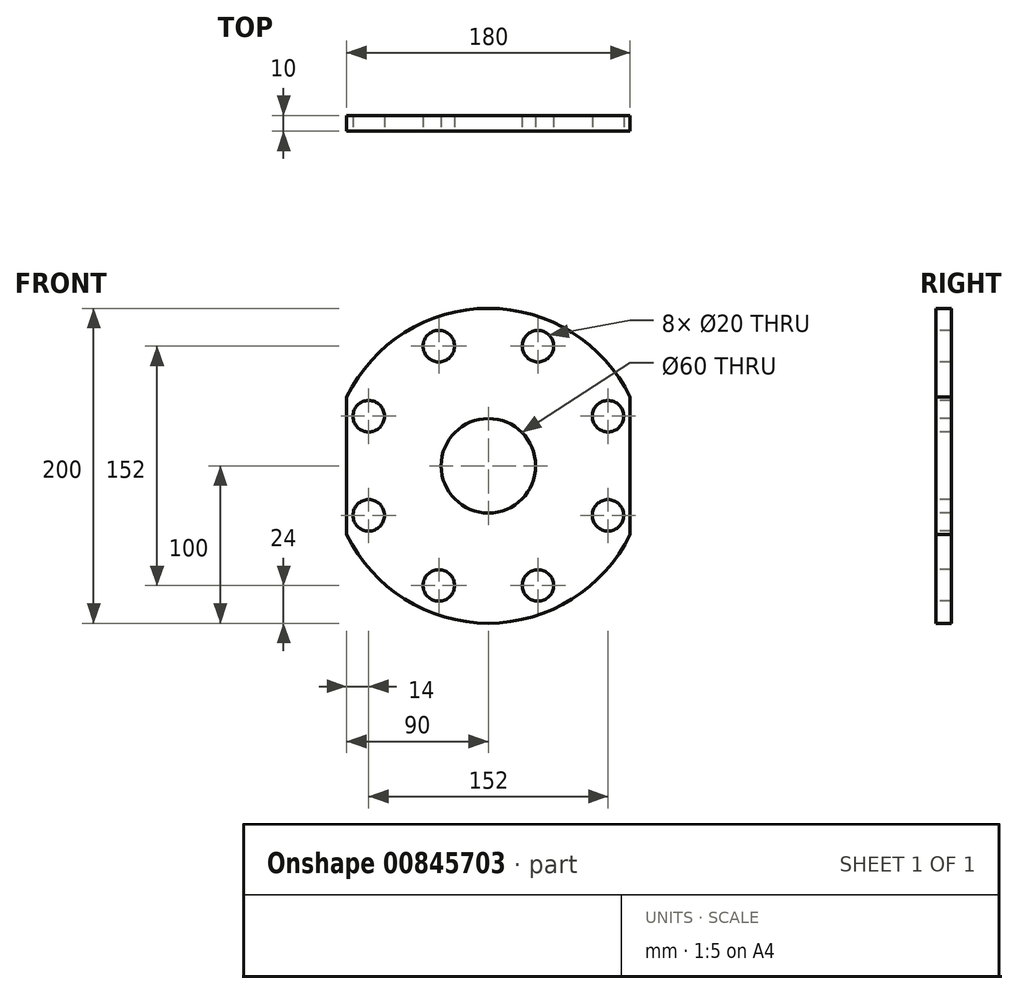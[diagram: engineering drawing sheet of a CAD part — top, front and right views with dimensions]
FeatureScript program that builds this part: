
annotation { "Feature Type Name" : "Feature", "Feature Type Description" : "" }
export const myFeature = defineFeature(function(context is Context, id is Id, definition is map)
    precondition{}
    {
        {
            var Q0;
            Q0=qCreatedBy(makeId("Front.planeOp"),FACE);
            var sketch = newSketch(context, id + "F0", { "sketchPlane" : qUnion([Q0])});
            skCircle(sketch, "E0", {"center": v(0, 0) * mm, "radius": 100 * mm});
            skSolve(sketch);
        }
        {
            var Q0;
            Q0=makeQuery(id+"F0.imprint","IMPRINT",FACE,{"disambiguationData":[TD([[makeQuery(id+"F0.imprint","IMPRINT",EDGE,{"derivedFrom":sQuery(id+"F0.wireOp",EDGE,"E0")}),1.0]])]});
            var sketch = newSketch(context, id + "F1", { "sketchPlane" : qUnion([Q0])});
            skLineSegment(sketch, "E1.bottom", {"start": v(90, 100) * mm, "end": v(-90, 100) * mm});
            skLineSegment(sketch, "E1.top", {"start": v(90, -100) * mm, "end": v(-90, -100) * mm});
            skLineSegment(sketch, "E1.left", {"start": v(90, 100) * mm, "end": v(90, -100) * mm});
            skLineSegment(sketch, "E1.right", {"start": v(-90, 100) * mm, "end": v(-90, -100) * mm});
            skPoint(sketch, "E1.middle", {"position": v(0, 0) * mm});
            skSolve(sketch);
        }
        {
            var Q0;
            Q0=qSketchRegion(id+"F0",true);
            extrude(context, id + "F2", {"entities" : qUnion([Q0]), "depth" : 10 * mm, "offsetDistance" : 25 * mm});
        }
        {
            var Q0;
            {var subQ0=sQuery(id+"F1.wireOp",EDGE,"E1.right");var subQ1=sQuery(id+"F1.wireOp",EDGE,"E1.bottom");var subQ2=makeQuery(id+"F1.imprint","INTERSECT",VERTEX,{"derivedFrom":[subQ1,subQ0]});Q0=makeQuery(id+"F1.imprint","IMPRINT",FACE,{"disambiguationData":[TD([[makeQuery(id+"F1.imprint","IMPRINT",EDGE,{"disambiguationData":[TD([[subQ2,1.0]])],"derivedFrom":subQ1}),1.0]])]});}
            var Q1;
            {var subQ0=sQuery(id+"F1.wireOp",EDGE,"E1.right");var subQ1=makeQuery(id+"F0.imprint","IMPRINT",EDGE,{"derivedFrom":sQuery(id+"F0.wireOp",EDGE,"E0")});var subQ2=makeQuery(id+"F1.imprint","INTERSECT",VERTEX,{"disambiguationData":[OD(0.0)],"derivedFrom":[subQ1,subQ0]});Q1=makeQuery(id+"F1.imprint","IMPRINT",FACE,{"disambiguationData":[TD([[makeQuery(id+"F1.imprint","IMPRINT",EDGE,{"disambiguationData":[TD([[subQ2,-1.0]])],"derivedFrom":subQ0}),-1.0]])]});}
            var Q2;
            {var subQ0=sQuery(id+"F1.wireOp",EDGE,"E1.left");var subQ1=makeQuery(id+"F0.imprint","IMPRINT",EDGE,{"derivedFrom":sQuery(id+"F0.wireOp",EDGE,"E0")});var subQ2=makeQuery(id+"F1.imprint","INTERSECT",VERTEX,{"disambiguationData":[OD(0.0)],"derivedFrom":[subQ1,subQ0]});Q2=makeQuery(id+"F1.imprint","IMPRINT",FACE,{"disambiguationData":[TD([[makeQuery(id+"F1.imprint","IMPRINT",EDGE,{"disambiguationData":[TD([[subQ2,-1.0]])],"derivedFrom":subQ0}),1.0]])]});}
            extrude(context, id + "F3", {"entities" : qUnion([Q0, Q1, Q2]), "operationType" : NewBodyOperationType.REMOVE, "endBound" : BoundingType.THROUGH_ALL, "depth" : 25 * mm, "offsetDistance" : 25 * mm});
        }
        {
            var Q0;
            Q0=makeQuery(id+"F2.opExtrude","CAP_FACE",FACE,{"disambiguationData":[OSD([sQuery(id+"F0.wireOp",EDGE,"E0")])],"isStart":false});
            var sketch = newSketch(context, id + "F4", { "sketchPlane" : qUnion([Q0])});
            skLineSegment(sketch, "E2", {"start": v(-90, 0) * mm, "end": v(90, 0) * mm, "construction": true});
            skLineSegment(sketch, "E3", {"start": v(0, 100) * mm, "end": v(0, -100) * mm, "construction": true});
            skCircle(sketch, "E4", {"center": v(-76, 31.48) * mm, "radius": 10 * mm});
            skLineSegment(sketch, "E5", {"start": v(70.71, -70.71) * mm, "end": v(0, 0) * mm, "construction": true});
            skLineSegment(sketch, "E6", {"start": v(0, 0) * mm, "end": v(-70.71, 70.71) * mm, "construction": true});
            skLineSegment(sketch, "E7", {"start": v(0, 0) * mm, "end": v(70.71, 70.71) * mm, "construction": true});
            skLineSegment(sketch, "E8", {"start": v(0, 0) * mm, "end": v(-70.71, -70.71) * mm, "construction": true});
            skLineSegment(sketch, "E9", {"start": v(0, 0) * mm, "end": v(-90, 37.28) * mm, "construction": true});
            skCircle(sketch, "E10.1.0", {"center": v(-76, -31.48) * mm, "radius": 10 * mm});
            skCircle(sketch, "E10.2.0", {"center": v(-31.48, -76) * mm, "radius": 10 * mm});
            skCircle(sketch, "E10.3.0", {"center": v(31.48, -76) * mm, "radius": 10 * mm});
            skCircle(sketch, "E10.4.0", {"center": v(76, -31.48) * mm, "radius": 10 * mm});
            skCircle(sketch, "E10.5.0", {"center": v(76, 31.48) * mm, "radius": 10 * mm});
            skCircle(sketch, "E10.6.0", {"center": v(31.48, 76) * mm, "radius": 10 * mm});
            skCircle(sketch, "E10.7.0", {"center": v(-31.48, 76) * mm, "radius": 10 * mm});
            skPoint(sketch, "E10.center", {"position": v(0, 0) * mm});
            skSolve(sketch);
        }
        {
            var Q0;
            Q0=qSketchRegion(id+"F4",true);
            extrude(context, id + "F5", {"entities" : qUnion([Q0]), "operationType" : NewBodyOperationType.REMOVE, "oppositeDirection" : true, "depth" : 25 * mm, "offsetDistance" : 25 * mm});
        }
        {
            var Q0;
            Q0=makeQuery(id+"F2.opExtrude","CAP_FACE",FACE,{"disambiguationData":[OSD([sQuery(id+"F0.wireOp",EDGE,"E0")])],"isStart":false});
            var sketch = newSketch(context, id + "F6", { "sketchPlane" : qUnion([Q0])});
            skCircle(sketch, "E11", {"center": v(0, 0) * mm, "radius": 30 * mm});
            skSolve(sketch);
        }
        {
            var Q0;
            Q0=makeQuery(id+"F6.imprint","IMPRINT",FACE,{"disambiguationData":[TD([[makeQuery(id+"F6.imprint","IMPRINT",EDGE,{"derivedFrom":sQuery(id+"F6.wireOp",EDGE,"E11")}),1.0]])]});
            extrude(context, id + "F7", {"entities" : qUnion([Q0]), "operationType" : NewBodyOperationType.REMOVE, "oppositeDirection" : true, "depth" : 25 * mm, "offsetDistance" : 25 * mm});
        }
    });
